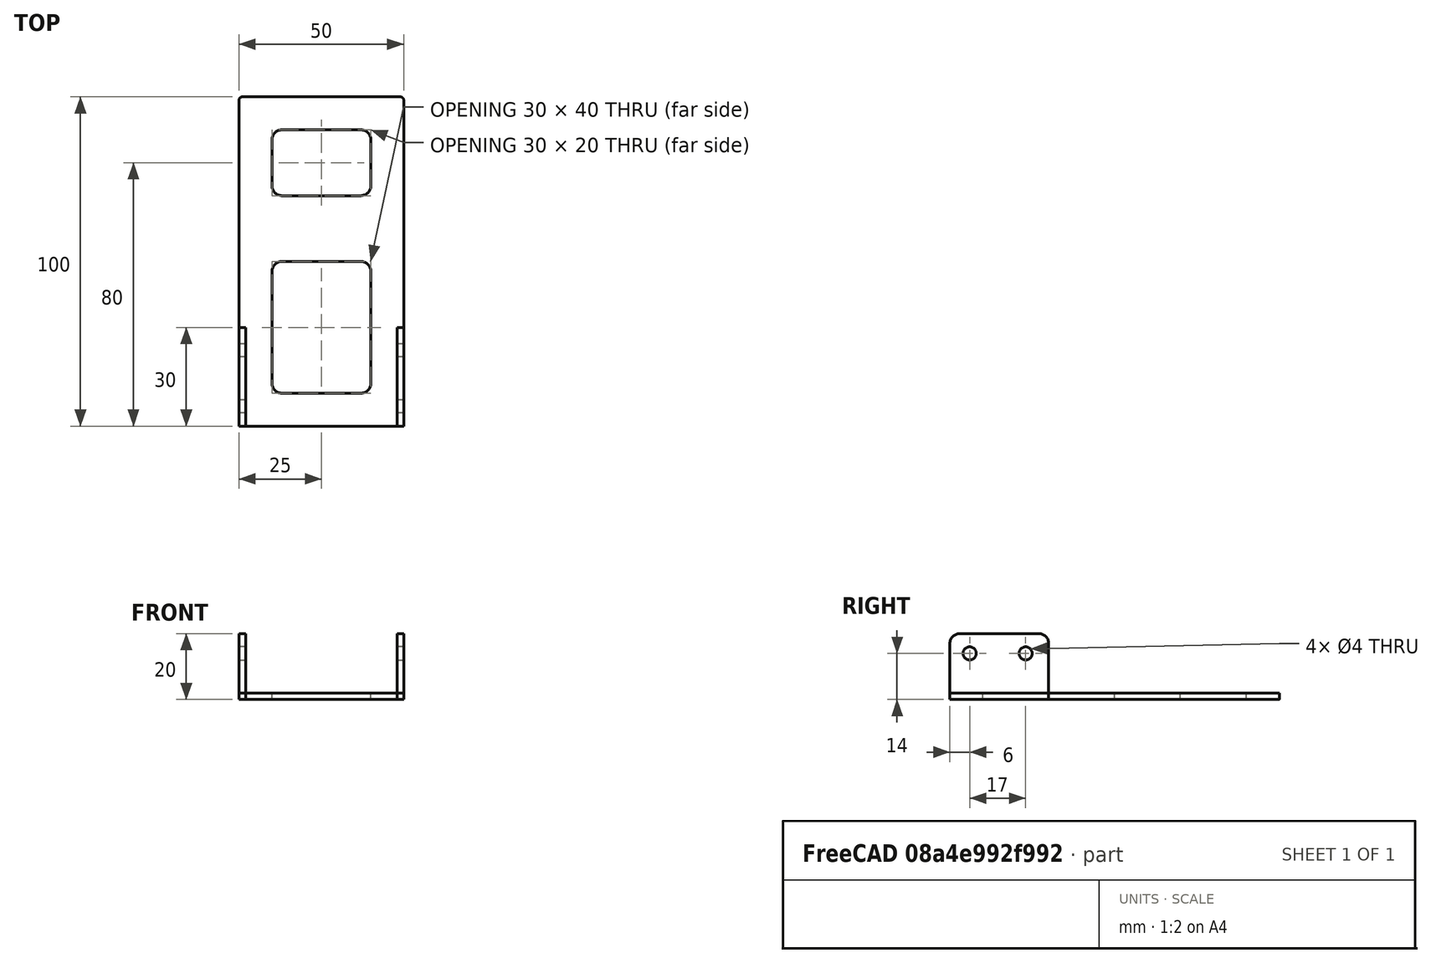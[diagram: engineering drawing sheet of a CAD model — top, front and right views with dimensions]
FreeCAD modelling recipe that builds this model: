
FCSTD DOCUMENT  (FreeCAD 1.0R39319 (Git))
Label: ojt1_t12r03_universal_support
License: All rights reserved
LicenseURL: https://en.wikipedia.org/wiki/All_rights_reserved
objects: Part::Box×5, Part::Fillet×5, Part::Cut×4, Part::Cylinder×4, Part::MultiFuse×2
note: 20 computed .brp shape members not serialized (recipe doc carries the construction recipe); baked Part::Feature solids carry a one-line shape summary decoded from their .brp

FEATURE [Part::Box] Box  label="Cub"
  AttacherType = Attacher::AttachEngine3D
  Height = 2
  Length = 50
  Width = 100
FEATURE [Part::Fillet] Fillet
  Base = -> Box
  EdgeLinks = -> Box [Edge3,Edge7]
  Edges = 2 edges r=1: [Edge3,Edge7]
FEATURE [Part::Box] Box001  label="Cub001"
  AttacherType = Attacher::AttachEngine3D
  Height = 3
  Length = 30
  Width = 20
FEATURE [Part::Fillet] Fillet001
  Base = -> Box001
  EdgeLinks = -> Box001 [Edge1,Edge3,Edge5,Edge7]
  Edges = 4 edges r=3: [Edge1,Edge3,Edge5,Edge7]
  Placement = pos=(10,70,0) rot=(0,0,1;0rad)
FEATURE [Part::Cut] Cut
  Base = -> Fillet
  Refine = true
  Tool = -> Fillet001
FEATURE [Part::Box] Box002  label="Cub002"
  AttacherType = Attacher::AttachEngine3D
  Height = 3
  Length = 30
  Width = 40
FEATURE [Part::Fillet] Fillet002
  Base = -> Box002
  EdgeLinks = -> Box002 [Edge1,Edge3,Edge5,Edge7]
  Edges = 4 edges r=3: [Edge1,Edge3,Edge5,Edge7]
  Placement = pos=(10,10,0) rot=(0,0,1;0rad)
FEATURE [Part::Cut] Cut001  label="base"
  Base = -> Cut
  Refine = true
  Tool = -> Fillet002
FEATURE [Part::Box] Box003  label="Cub003"
  AttacherType = Attacher::AttachEngine3D
  Height = 20
  Length = 2
  Width = 30
FEATURE [Part::Fillet] Fillet003
  Base = -> Box003
  EdgeLinks = -> Box003 [Edge10,Edge12]
  Edges = 2 edges r=3: [Edge10,Edge12]
FEATURE [Part::Cylinder] Cylinder  label="Cilindre"
  Angle = 360
  AttacherType = Attacher::AttachEngine3D
  FirstAngle = 0
  Height = 3
  Placement = pos=(0,6,14) rot=(0,1,0;1.5708rad)
  Radius = 2
  SecondAngle = 0
FEATURE [Part::Cylinder] Cylinder001  label="Cilindre001"
  Angle = 360
  AttacherType = Attacher::AttachEngine3D
  FirstAngle = 0
  Height = 3
  Placement = pos=(0,23,14) rot=(0,1,0;1.5708rad)
  Radius = 2
  SecondAngle = 0
FEATURE [Part::MultiFuse] Fusion
  Refine = true
  Shapes = -> [Cylinder,Cylinder001]
FEATURE [Part::Cut] Cut002  label="costat"
  Base = -> Fillet003
  Refine = true
  Tool = -> Fusion
FEATURE [Part::Box] Box004  label="Cub004"
  AttacherType = Attacher::AttachEngine3D
  Height = 20
  Length = 2
  Width = 30
FEATURE [Part::Cylinder] Cylinder002  label="Cilindre002"
  Angle = 360
  AttacherType = Attacher::AttachEngine3D
  FirstAngle = 0
  Height = 3
  Placement = pos=(0,6,14) rot=(0,1,0;1.5708rad)
  Radius = 2
  SecondAngle = 0
FEATURE [Part::Cylinder] Cylinder003  label="Cilindre003"
  Angle = 360
  AttacherType = Attacher::AttachEngine3D
  FirstAngle = 0
  Height = 3
  Placement = pos=(0,23,14) rot=(0,1,0;1.5708rad)
  Radius = 2
  SecondAngle = 0
FEATURE [Part::Fillet] Fillet004
  Base = -> Box004
  EdgeLinks = -> Box004 [Edge10,Edge12]
  Edges = 2 edges r=3: [Edge10,Edge12]
FEATURE [Part::MultiFuse] Fusion001
  Refine = true
  Shapes = -> [Cylinder002,Cylinder003]
FEATURE [Part::Cut] Cut003  label="costat001"
  Base = -> Fillet004
  Placement = pos=(48,0,0) rot=(0,0,1;0rad)
  Refine = true
  Tool = -> Fusion001
